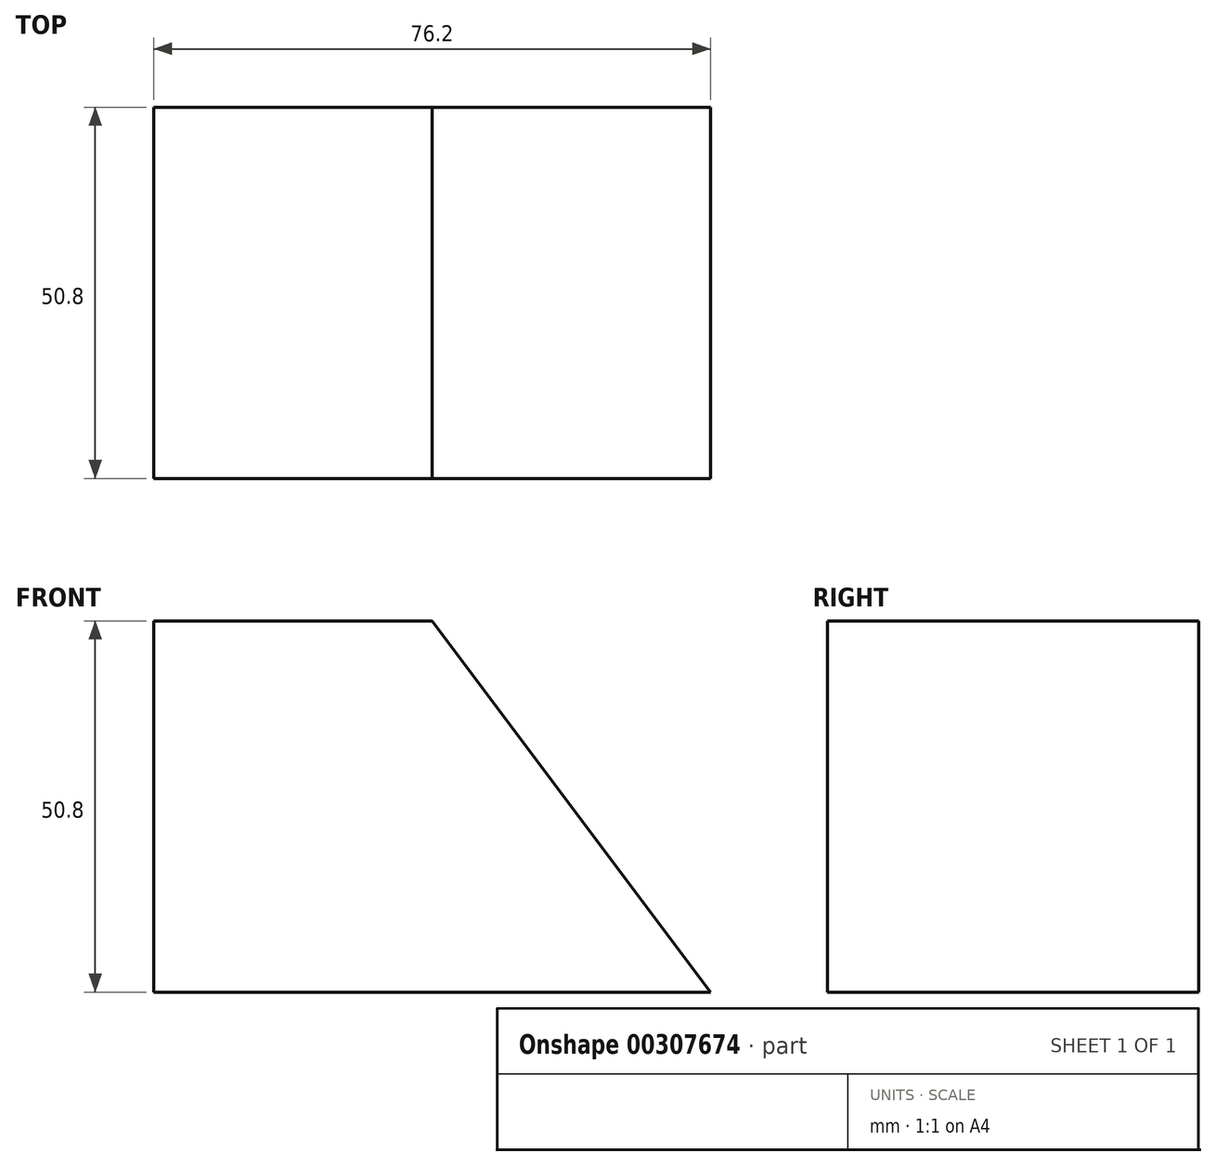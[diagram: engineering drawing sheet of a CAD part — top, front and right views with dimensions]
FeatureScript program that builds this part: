
annotation { "Feature Type Name" : "Feature", "Feature Type Description" : "" }
export const myFeature = defineFeature(function(context is Context, id is Id, definition is map)
    precondition{}
    {
        {
            var Q0;
            Q0=qCreatedBy(makeId("Front.planeOp"),FACE);
            var sketch = newSketch(context, id + "F0", { "sketchPlane" : qUnion([Q0])});
            skLineSegment(sketch, "E0", {"start": v(24.89, -36.28) * mm, "end": v(-51.31, -36.28) * mm});
            skLineSegment(sketch, "E1", {"start": v(-51.31, -36.28) * mm, "end": v(-51.31, 14.52) * mm});
            skLineSegment(sketch, "E2", {"start": v(-51.31, 14.52) * mm, "end": v(-13.21, 14.52) * mm});
            skLineSegment(sketch, "E3", {"start": v(-13.21, 14.52) * mm, "end": v(24.89, -36.28) * mm});
            skSolve(sketch);
        }
        {
            var Q0;
            Q0=makeQuery(id+"F0.imprint","IMPRINT",FACE,{"disambiguationData":[TD([[makeQuery(id+"F0.imprint","IMPRINT",EDGE,{"derivedFrom":sQuery(id+"F0.wireOp",EDGE,"E0")}),-1.0]])]});
            extrude(context, id + "F1", {"entities" : qUnion([Q0]), "depth" : 50.8 * mm});
        }
    });
